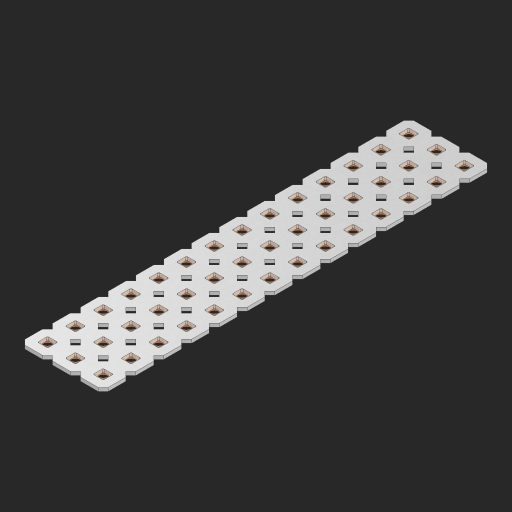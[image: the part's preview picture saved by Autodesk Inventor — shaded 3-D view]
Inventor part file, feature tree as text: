
AUTODESK INVENTOR PART (.ipt)
format: ipt  version: 2023 (Build 270158000, 158)  size: 764,416 bytes
history: native  units: in
note: dims shown in document units (in); Inventor stores cm internally (conversion verified against a paired STEP export)
features: other x43, extrude x41, sketch x2, pattern_linear x1
ambient origin geometry x8: Origin, YZ Plane, XZ Plane, XY Plane, X Axis, Y Axis, Z Axis, Center Point
bodies: Solid1 (feature_tree), Body (feature_tree)
feature tree (87):
  pattern_linear  "Rectangular Pattern1"  Spacing1=0.09in  [1 undecoded]
  sketch  "Sketch1"  dims[d1=0.5in]
  sketch  "Sketch2"  dims[d2=0.182in d3=0.09in d4=0.09in d5=0.09in d6=0.09in d7=0.09in d8=0.09in d9=0.09in d10=0.09in d11=0.02in d13=0.0in d14=0.172in d15=0.0625in d16=0.0in d19=0.5in d22=0.5in]
  other  "Srf1"
  other  "Srf126"
  other  "Srf127"
  other  "Srf128"
  other  "Srf129"
  other  "Srf130"
  other  "Srf131"
  other  "Srf250"
  other  "Srf251"
  other  "Srf252"
  other  "Srf253"
  other  "Srf254"
  other  "Srf255"
  other  "Srf256"
  other  "Srf268"
  other  "Srf269"
  other  "Srf270"
  other  "Srf271"
  other  "Srf272"
  other  "Srf273"
  other  "Srf274"
  other  "Srf275"
  other  "Srf276"
  other  "Srf277"
  other  "Srf278"
  other  "Srf279"
  other  "Srf280"
  other  "Srf281"
  other  "Srf293"
  other  "Srf294"
  other  "Srf295"
  other  "Srf296"
  other  "Srf297"
  other  "Srf298"
  other  "Srf299"
  other  "Srf300"
  other  "Srf301"
  other  "Srf302"
  other  "Srf303"
  other  "Srf304"
  other  "Srf305"
  other  "Srf306"
  other  "Circle"
  extrude  "ExtrusionSrf126"  Depth=0.09in
  extrude  "ExtrusionSrf127"  Depth=0.09in
  extrude  "ExtrusionSrf128"  Depth=0.09in
  extrude  "ExtrusionSrf129"  Depth=0.09in
  extrude  "ExtrusionSrf130"  Depth=0.09in
  extrude  "ExtrusionSrf131"  Depth=0.09in
  extrude  "ExtrusionSrf250"  Depth=0.09in
  extrude  "ExtrusionSrf251"  Depth=0.02in
  extrude  "ExtrusionSrf252"  TaperAngle=0.0deg  [1 undecoded]
  extrude  "ExtrusionSrf253"  Depth=0.5in
  extrude  "ExtrusionSrf254"  Depth=0.0625in TaperAngle=0.0deg
  extrude  "ExtrusionSrf255"  Depth=0.5in
  extrude  "ExtrusionSrf256"  Depth=0.5in
  extrude  "ExtrusionSrf268"  [1 undecoded]
  extrude  "ExtrusionSrf269"  [1 undecoded]
  extrude  "ExtrusionSrf270"  [1 undecoded]
  extrude  "ExtrusionSrf271"  [1 undecoded]
  extrude  "ExtrusionSrf272"  [1 undecoded]
  extrude  "ExtrusionSrf273"  [1 undecoded]
  extrude  "ExtrusionSrf274"  [1 undecoded]
  extrude  "ExtrusionSrf275"  [1 undecoded]
  extrude  "ExtrusionSrf276"  [1 undecoded]
  extrude  "ExtrusionSrf277"  [1 undecoded]
  extrude  "ExtrusionSrf278"  [1 undecoded]
  extrude  "ExtrusionSrf279"  [1 undecoded]
  extrude  "ExtrusionSrf280"  [1 undecoded]
  extrude  "ExtrusionSrf281"  [1 undecoded]
  extrude  "ExtrusionSrf293"  [1 undecoded]
  extrude  "ExtrusionSrf294"  [1 undecoded]
  extrude  "ExtrusionSrf295"  [1 undecoded]
  extrude  "ExtrusionSrf296"  [1 undecoded]
  extrude  "ExtrusionSrf297"  [1 undecoded]
  extrude  "ExtrusionSrf298"  [1 undecoded]
  extrude  "ExtrusionSrf299"  [1 undecoded]
  extrude  "ExtrusionSrf300"  [1 undecoded]
  extrude  "ExtrusionSrf301"  [1 undecoded]
  extrude  "ExtrusionSrf302"  [1 undecoded]
  extrude  "ExtrusionSrf303"  [1 undecoded]
  extrude  "ExtrusionSrf304"  [1 undecoded]
  extrude  "ExtrusionSrf305"  [1 undecoded]
  extrude  "ExtrusionSrf306"  [1 undecoded]
note: 30 required parameter values undecoded (feature->parameter linkage not recoverable at this tier; creation-order binding heuristic only, values carry confidence <= 0.55)
